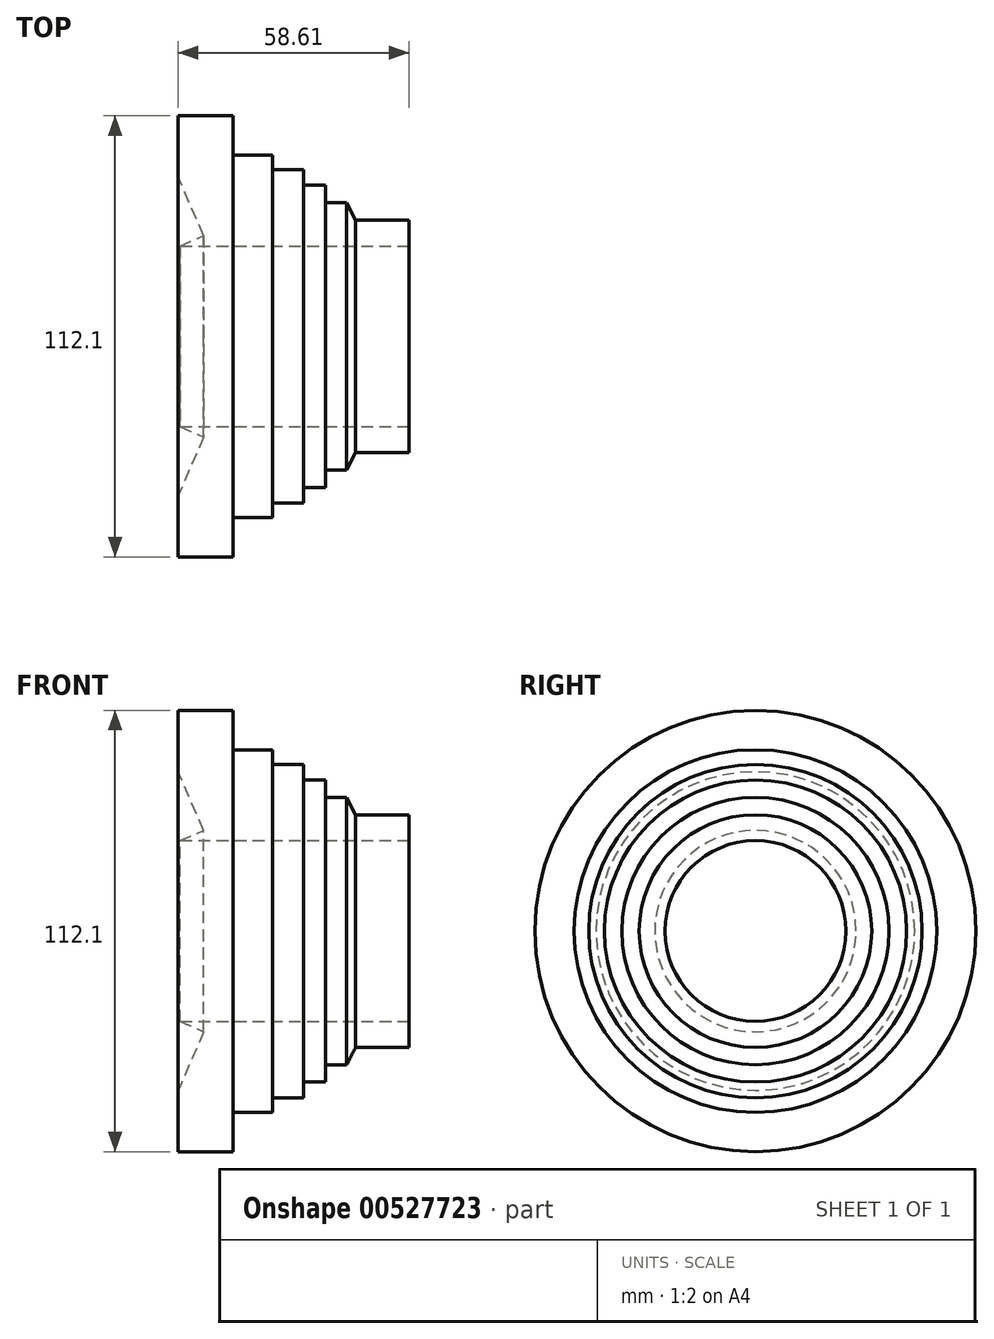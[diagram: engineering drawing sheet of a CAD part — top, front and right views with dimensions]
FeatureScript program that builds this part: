
annotation { "Feature Type Name" : "Feature", "Feature Type Description" : "" }
export const myFeature = defineFeature(function(context is Context, id is Id, definition is map)
    precondition{}
    {
        {
            var Q0;
            Q0=qCreatedBy(makeId("Front.planeOp"),FACE);
            var sketch = newSketch(context, id + "F0", { "sketchPlane" : qUnion([Q0])});
            skLineSegment(sketch, "E0", {"start": v(0, 0) * mm, "end": v(-74.9, 0) * mm});
            skLineSegment(sketch, "E1", {"start": v(0, 29.54) * mm, "end": v(-13.5, 29.54) * mm});
            skLineSegment(sketch, "E2", {"start": v(-13.5, 29.54) * mm, "end": v(-15.82, 33.96) * mm});
            skLineSegment(sketch, "E3", {"start": v(-15.82, 33.96) * mm, "end": v(-21.17, 33.96) * mm});
            skLineSegment(sketch, "E4", {"start": v(-21.17, 33.96) * mm, "end": v(-21.17, 38.38) * mm});
            skLineSegment(sketch, "E5", {"start": v(-21.17, 38.38) * mm, "end": v(-26.75, 38.38) * mm});
            skLineSegment(sketch, "E6", {"start": v(-26.75, 38.38) * mm, "end": v(-26.75, 42.33) * mm});
            skLineSegment(sketch, "E7", {"start": v(-26.75, 42.33) * mm, "end": v(-34.66, 42.33) * mm});
            skLineSegment(sketch, "E8", {"start": v(-34.66, 46.05) * mm, "end": v(-34.66, 42.33) * mm});
            skLineSegment(sketch, "E9", {"start": v(-34.66, 46.05) * mm, "end": v(-44.66, 46.05) * mm});
            skLineSegment(sketch, "E10", {"start": v(-44.66, 46.05) * mm, "end": v(-44.66, 56.05) * mm});
            skLineSegment(sketch, "E11", {"start": v(-44.66, 56.05) * mm, "end": v(-58.61, 56.05) * mm});
            skLineSegment(sketch, "E12", {"start": v(-58.61, 56.05) * mm, "end": v(-58.61, 40.47) * mm});
            skLineSegment(sketch, "E13", {"start": v(-58.61, 40.47) * mm, "end": v(-52.1, 25.58) * mm});
            skLineSegment(sketch, "E14", {"start": v(-52.1, 25.58) * mm, "end": v(-58.07, 22.97) * mm});
            skLineSegment(sketch, "E15", {"start": v(-58.07, 22.97) * mm, "end": v(0, 22.97) * mm});
            skLineSegment(sketch, "E16", {"start": v(0, 22.97) * mm, "end": v(0, 29.54) * mm});
            skSolve(sketch);
        }
        {
            var Q0;
            Q0=makeQuery(id+"F0.imprint","IMPRINT",FACE,{"disambiguationData":[TD([[makeQuery(id+"F0.imprint","IMPRINT",EDGE,{"derivedFrom":sQuery(id+"F0.wireOp",EDGE,"E1")}),1.0]])]});
            var Q1;
            Q1=sQuery(id+"F0.wireOp",EDGE,"E0");
            revolve(context, id + "F1", {"entities" : qUnion([Q0]), "axis" : qUnion([Q1]), "revolveType" : RevolveType.FULL});
        }
    });
